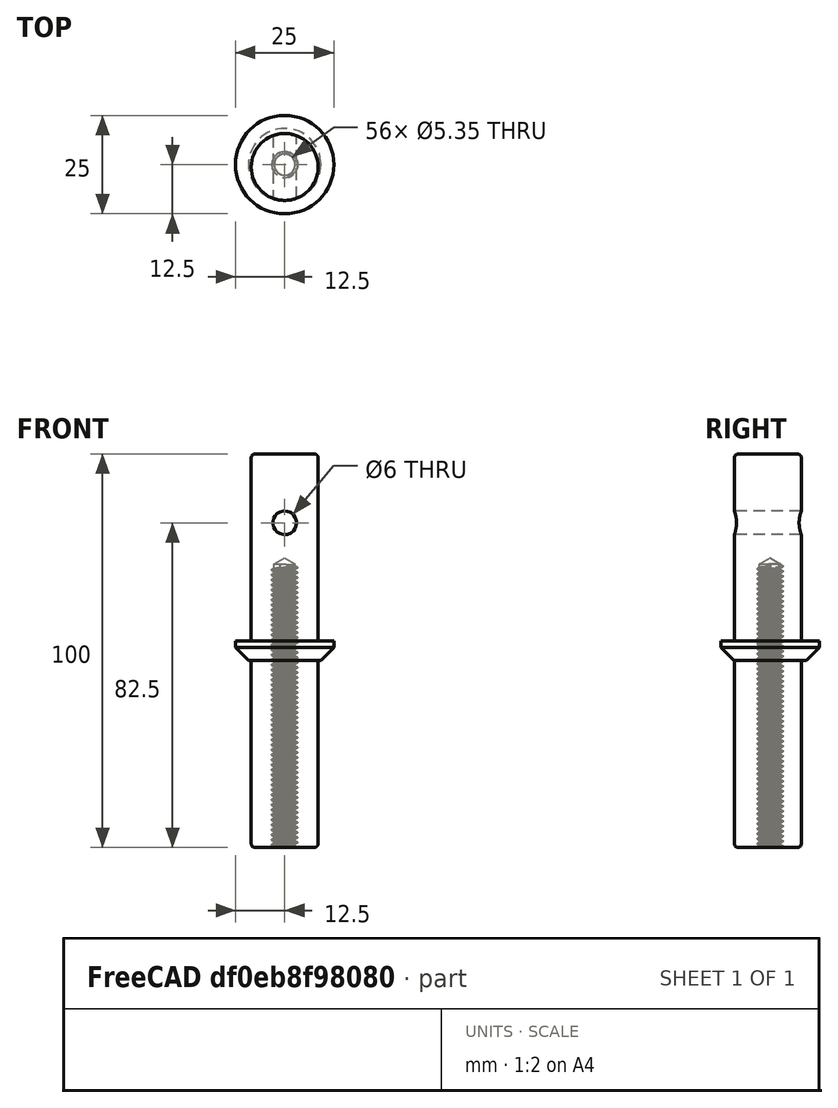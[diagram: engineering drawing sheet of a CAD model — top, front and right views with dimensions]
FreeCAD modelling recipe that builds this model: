
FCSTD DOCUMENT  (FreeCAD 1.0R39109 (Git))
Label: adapt-tuyaux
License: All rights reserved
LicenseURL: https://en.wikipedia.org/wiki/All_rights_reserved
objects: TechDraw::DrawViewDimension×6, Sketcher::SketchObject×4, TechDraw::DrawProjGroupItem×3, PartDesign::Pad×2, PartDesign::Chamfer×1, PartDesign::Fillet×1, TechDraw::DrawSVGTemplate×1, PartDesign::Pocket×1, PartDesign::Hole×1, PartDesign::Body×1, TechDraw::DrawProjGroup×1, TechDraw::DrawPage×1
note: 37 computed .brp shape members not serialized (recipe doc carries the construction recipe); baked Part::Feature solids carry a one-line shape summary decoded from their .brp

FEATURE [Sketcher::SketchObject] Sketch
  ArcFitTolerance = 1e-06
  AttachmentSupport = -> [XY_Plane]
  FullyConstrained = false
  MakeInternals = false
  MapMode = 5
  sketch-geometry (1):
    g0: Circle CenterX=0 CenterY=-0.600294 CenterZ=0 NormalX=0 NormalY=0 NormalZ=1 AngleXU=0 Radius=8.5
  constraints (2):
    c: Diameter(g0) = 17
    c: PointOnObject(g0,g-2)
FEATURE [PartDesign::Pad] Pad
  Direction = (0,0,1)
  Length = 100
  Length2 = 10
  Profile = -> Sketch
  ReferenceAxis = -> Sketch [N_Axis]
  Refine = true
  Suppressed = false
  Type = 0
FEATURE [Sketcher::SketchObject] Sketch001
  ArcFitTolerance = 1e-06
  AttachmentOffset = pos=(0,0,47.5) rot=(0,0,1;0rad)
  AttachmentSupport = -> [XY_Plane]
  FullyConstrained = true
  MakeInternals = false
  MapMode = 5
  Placement = pos=(0,0,47.5) rot=(0,0,1;0rad)
  sketch-geometry (1):
    g0: Circle CenterX=0 CenterY=0 CenterZ=0 NormalX=0 NormalY=0 NormalZ=1 AngleXU=0 Radius=12.5
  constraints (2):
    c: Diameter(g0) = 25
    c: Coincident(g0,g-1)
FEATURE [PartDesign::Pad] Pad001
  BaseFeature = -> Pad
  Direction = (0,0,1)
  Length = 5
  Length2 = 10
  Profile = -> Sketch001
  ReferenceAxis = -> Sketch001 [N_Axis]
  Refine = true
  Suppressed = false
  Type = 0
FEATURE [PartDesign::Chamfer] Chamfer
  Angle = 45
  Base = -> Pad001 [Edge4]
  BaseFeature = -> Pad001
  ChamferType = 0
  FlipDirection = false
  Refine = true
  Size = 3.3
  Size2 = 1
  SupportTransform = false
  Suppressed = false
  UseAllEdges = false
FEATURE [PartDesign::Fillet] Fillet
  Base = -> Chamfer [Edge11,Edge5]
  BaseFeature = -> Chamfer
  Radius = 1
  Refine = true
  SupportTransform = false
  Suppressed = false
  UseAllEdges = false
FEATURE [TechDraw::DrawSVGTemplate] Template  label="Modèle"
  Height = 210
  Orientation = 1
  Template = C:/Program Files/FreeCAD 1.0/data/Mod/TechDraw/Templates/Default_Template_A4_Landscape.svg
  Width = 297
FEATURE [Sketcher::SketchObject] Sketch005
  ArcFitTolerance = 1e-06
  AttachmentSupport = -> [XZ_Plane]
  FullyConstrained = true
  MakeInternals = false
  MapMode = 5
  Placement = pos=(0,0,0) rot=(1,0,0;1.5708rad)
  sketch-geometry (1):
    g0: Circle CenterX=0 CenterY=82.5 CenterZ=0 NormalX=0 NormalY=0 NormalZ=1 AngleXU=0 Radius=3
  constraints (3):
    c: Diameter(g0) = 6
    c: PointOnObject(g0,g-2)
    c: DistanceY(g-1,g0) = 82.5
FEATURE [PartDesign::Pocket] Pocket002
  BaseFeature = -> Fillet
  Direction = (0,1,-2e-16)
  Length = 30
  Length2 = 5
  Midplane = true
  Profile = -> Sketch005
  ReferenceAxis = -> Sketch005 [N_Axis]
  Refine = true
  Suppressed = false
  Type = 0
FEATURE [Sketcher::SketchObject] Sketch006
  ArcFitTolerance = 1e-06
  AttachmentSupport = -> [XY_Plane]
  FullyConstrained = false
  MakeInternals = false
  MapMode = 5
  sketch-geometry (1):
    g0: Circle CenterX=0 CenterY=0 CenterZ=0 NormalX=0 NormalY=0 NormalZ=1 AngleXU=0 Radius=2.4602
  constraints (1):
    c: Coincident(g0,g-1)
FEATURE [PartDesign::Hole] Hole
  BaseFeature = -> Pocket002
  CustomThreadClearance = 0.25
  Depth = 72
  DepthType = 0
  Diameter = 5.35
  DrillForDepth = false
  DrillPoint = 1
  DrillPointAngle = 118
  HoleCutCountersinkAngle = 90
  HoleCutCustomValues = false
  HoleCutDepth = 0
  HoleCutDiameter = 7.2
  HoleCutType = 0
  ModelThread = true
  Profile = -> Sketch006
  Refine = true
  Reversed = true
  Suppressed = false
  Tapered = false
  TaperedAngle = 90
  ThreadClass = 0
  ThreadDepth = 72
  ThreadDepthType = 0
  ThreadDirection = 0
  ThreadFit = 0
  ThreadSize = 9
  ThreadType = 3
  Threaded = true
  UseCustomThreadClearance = true
FEATURE [PartDesign::Body] Body
  AllowCompound = false
  Group = -> [Sketch,Pad,Sketch001,Pad001,Chamfer,Fillet,Sketch005,Pocket002,Sketch006,Hole]
  Origin = -> Origin
  Tip = -> Hole
FEATURE [TechDraw::DrawProjGroupItem] View  label="Front"
  CoarseView = false
  Direction = (0,-1,0)
  Focus = 100
  HardHidden = false
  IsoCount = 0
  IsoHidden = false
  IsoVisible = false
  LockPosition = true
  Perspective = false
  Rotation = 0
  RotationVector = (1,0,0)
  ScaleType = 2
  ScrubCount = 1
  SeamHidden = false
  SeamVisible = false
  SmoothHidden = false
  SmoothVisible = true
  Source = -> [Body]
  Type = 0
  X = 0
  XDirection = (1,0,0)
  Y = 0
FEATURE [TechDraw::DrawProjGroupItem] ProjItem  label="Avant en haut à gauche"
  CoarseView = false
  Direction = (-0.57735,-0.57735,0.57735)
  Focus = 100
  HardHidden = false
  IsoCount = 0
  IsoHidden = false
  IsoVisible = false
  LockPosition = false
  Perspective = false
  Rotation = 0
  RotationVector = (1,0,0)
  ScaleType = 0
  ScrubCount = 1
  SeamHidden = false
  SeamVisible = false
  SmoothHidden = false
  SmoothVisible = true
  Source = -> [Body]
  Type = 6
  X = 40
  XDirection = (0.707107,-0.707107,0)
  Y = -110.338
FEATURE [TechDraw::DrawProjGroupItem] ProjItem001  label="Dessous"
  CoarseView = false
  Direction = (0,0,-1)
  Focus = 100
  HardHidden = false
  IsoCount = 0
  IsoHidden = false
  IsoVisible = false
  LockPosition = false
  Perspective = false
  Rotation = 0
  RotationVector = (1,0,0)
  ScaleType = 0
  ScrubCount = 1
  SeamHidden = false
  SeamVisible = false
  SmoothHidden = false
  SmoothVisible = true
  Source = -> [Body]
  Type = 5
  X = 0
  XDirection = (1,0,0)
  Y = 77.5
FEATURE [TechDraw::DrawProjGroup] ProjGroup
  Anchor = -> View
  AutoDistribute = true
  LockPosition = false
  ProjectionType = 0
  Rotation = 0
  ScaleType = 0
  Source = -> [Body]
  Views = -> [View,ProjItem,ProjItem001]
  X = 148.5
  Y = 105
  spacingX = 15
  spacingY = 15
FEATURE [TechDraw::DrawViewDimension] Dimension  label="Cote"
  AngleOverride = false
  Arbitrary = false
  ArbitraryTolerances = false
  BoxCorners = (2) [(-12.5,-12.5,0),(12.5,12.5,0)]
  EqualTolerance = true
  ExtensionAngle = 0
  FormatSpec = ⌀%.2w
  FormatSpecOverTolerance = %+.2w
  FormatSpecUnderTolerance = %+.2w
  Inverted = false
  LineAngle = 0
  LockPosition = false
  MeasureType = 1
  OverTolerance = 0
  References2D = -> [ProjItem001]
  Rotation = 0
  ScaleType = 0
  TheoreticalExact = false
  Type = 5
  UnderTolerance = 0
  X = -36.7073
  Y = 2.38361
FEATURE [TechDraw::DrawViewDimension] Dimension001  label="Cote001"
  AngleOverride = false
  Arbitrary = false
  ArbitraryTolerances = false
  BoxCorners = (2) [(-12.5,-12.5,0),(12.5,12.5,0)]
  EqualTolerance = true
  ExtensionAngle = 0
  FormatSpec = ⌀%.2w
  FormatSpecOverTolerance = %+.2w
  FormatSpecUnderTolerance = %+.2w
  Inverted = false
  LineAngle = 0
  LockPosition = false
  MeasureType = 1
  OverTolerance = 0
  References2D = -> [ProjItem001]
  Rotation = 0
  ScaleType = 0
  TheoreticalExact = false
  Type = 5
  UnderTolerance = 0
  X = -35.7086
  Y = -11.9032
FEATURE [TechDraw::DrawViewDimension] Dimension002  label="Cote002"
  AngleOverride = false
  Arbitrary = false
  ArbitraryTolerances = false
  BoxCorners = (2) [(-12.5,-50,-1e-07),(12.5,50,1e-07)]
  EqualTolerance = true
  ExtensionAngle = 0
  FormatSpec = %.2w
  FormatSpecOverTolerance = %+.2w
  FormatSpecUnderTolerance = %+.2w
  Inverted = false
  LineAngle = 0
  LockPosition = false
  MeasureType = 1
  OverTolerance = 0
  References2D = -> [View]
  Rotation = 0
  ScaleType = 0
  TheoreticalExact = false
  Type = 0
  UnderTolerance = 0
  X = -46.3063
  Y = 0
FEATURE [TechDraw::DrawViewDimension] Dimension003  label="Cote003"
  AngleOverride = false
  Arbitrary = false
  ArbitraryTolerances = false
  BoxCorners = (2) [(-12.5,-50,-1e-07),(12.5,50,1e-07)]
  EqualTolerance = true
  ExtensionAngle = 0
  FormatSpec = %.2w
  FormatSpecOverTolerance = %+.2w
  FormatSpecUnderTolerance = %+.2w
  Inverted = false
  LineAngle = 0
  LockPosition = false
  MeasureType = 1
  OverTolerance = 0
  References2D = -> [View]
  Rotation = 0
  ScaleType = 0
  TheoreticalExact = false
  Type = 0
  UnderTolerance = 0
  X = 22.779
  Y = 26.25
FEATURE [TechDraw::DrawViewDimension] Dimension004  label="Cote004"
  AngleOverride = false
  Arbitrary = false
  ArbitraryTolerances = false
  BoxCorners = (2) [(-12.5,-50,-1e-07),(12.5,50,1e-07)]
  EqualTolerance = true
  ExtensionAngle = 0
  FormatSpec = %.2w
  FormatSpecOverTolerance = %+.2w
  FormatSpecUnderTolerance = %+.2w
  Inverted = false
  LineAngle = 0
  LockPosition = false
  MeasureType = 1
  OverTolerance = 0
  References2D = -> [View]
  Rotation = 0
  ScaleType = 0
  TheoreticalExact = false
  Type = 0
  UnderTolerance = 0
  X = -22.2754
  Y = -18
FEATURE [TechDraw::DrawViewDimension] Dimension005
  AngleOverride = false
  Arbitrary = false
  ArbitraryTolerances = false
  BoxCorners = (2) [(-12.5,-50,-1e-07),(12.5,50,1e-07)]
  EqualTolerance = true
  ExtensionAngle = 0
  FormatSpec = %.2w
  FormatSpecOverTolerance = %+.2w
  FormatSpecUnderTolerance = %+.2w
  Inverted = false
  LineAngle = 0
  LockPosition = false
  MeasureType = 1
  OverTolerance = 0
  References2D = -> [View]
  Rotation = 0
  ScaleType = 0
  TheoreticalExact = false
  Type = 0
  UnderTolerance = 0
  X = -26.4783
  Y = 17.5
FEATURE [TechDraw::DrawPage] Page  label="Feuille"
  KeepUpdated = true
  NextBalloonIndex = 1
  ProjectionType = 0
  Template = -> Template
  Views = -> [ProjGroup,Dimension,Dimension001,Dimension002,Dimension003,Dimension004,Dimension005]
